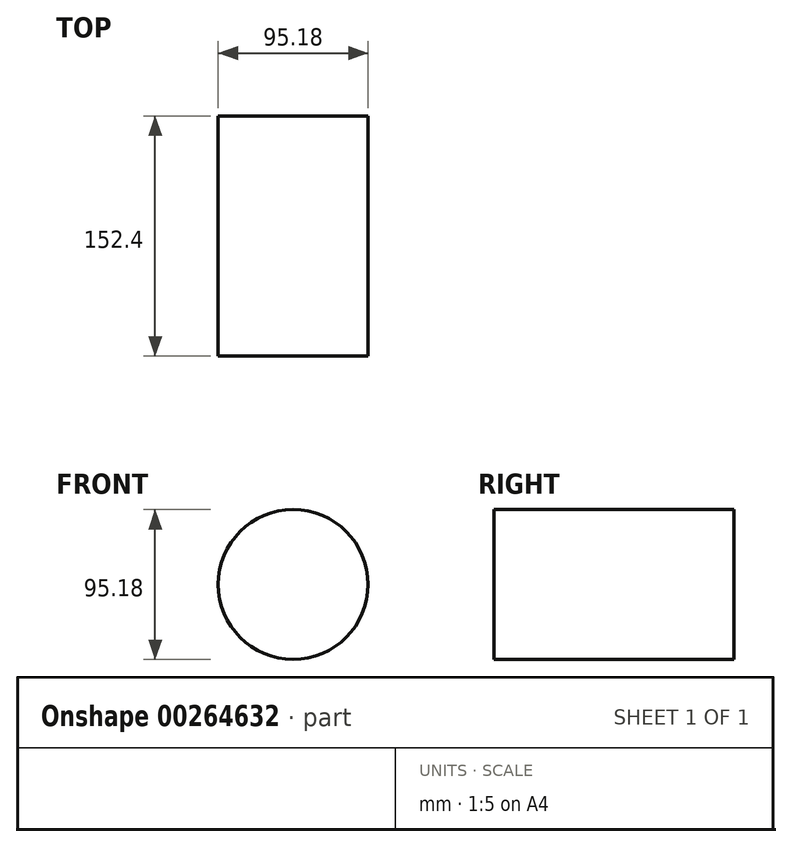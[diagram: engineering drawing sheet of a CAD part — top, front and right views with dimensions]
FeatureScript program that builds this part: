
annotation { "Feature Type Name" : "Feature", "Feature Type Description" : "" }
export const myFeature = defineFeature(function(context is Context, id is Id, definition is map)
    precondition{}
    {
        {
            var Q0;
            Q0=qCreatedBy(makeId("Front.planeOp"),FACE);
            var sketch = newSketch(context, id + "F0", { "sketchPlane" : qUnion([Q0])});
            skCircle(sketch, "E0", {"center": v(0, 0) * mm, "radius": 47.59 * mm});
            skSolve(sketch);
        }
        {
            var Q0;
            Q0=makeQuery(id+"F0.imprint","IMPRINT",FACE,{"disambiguationData":[TD([[makeQuery(id+"F0.imprint","IMPRINT",EDGE,{"derivedFrom":sQuery(id+"F0.wireOp",EDGE,"E0")}),1.0]])]});
            extrude(context, id + "F1", {"entities" : qUnion([Q0]), "depth" : 152.4 * mm, "symmetric" : true});
        }
    });
